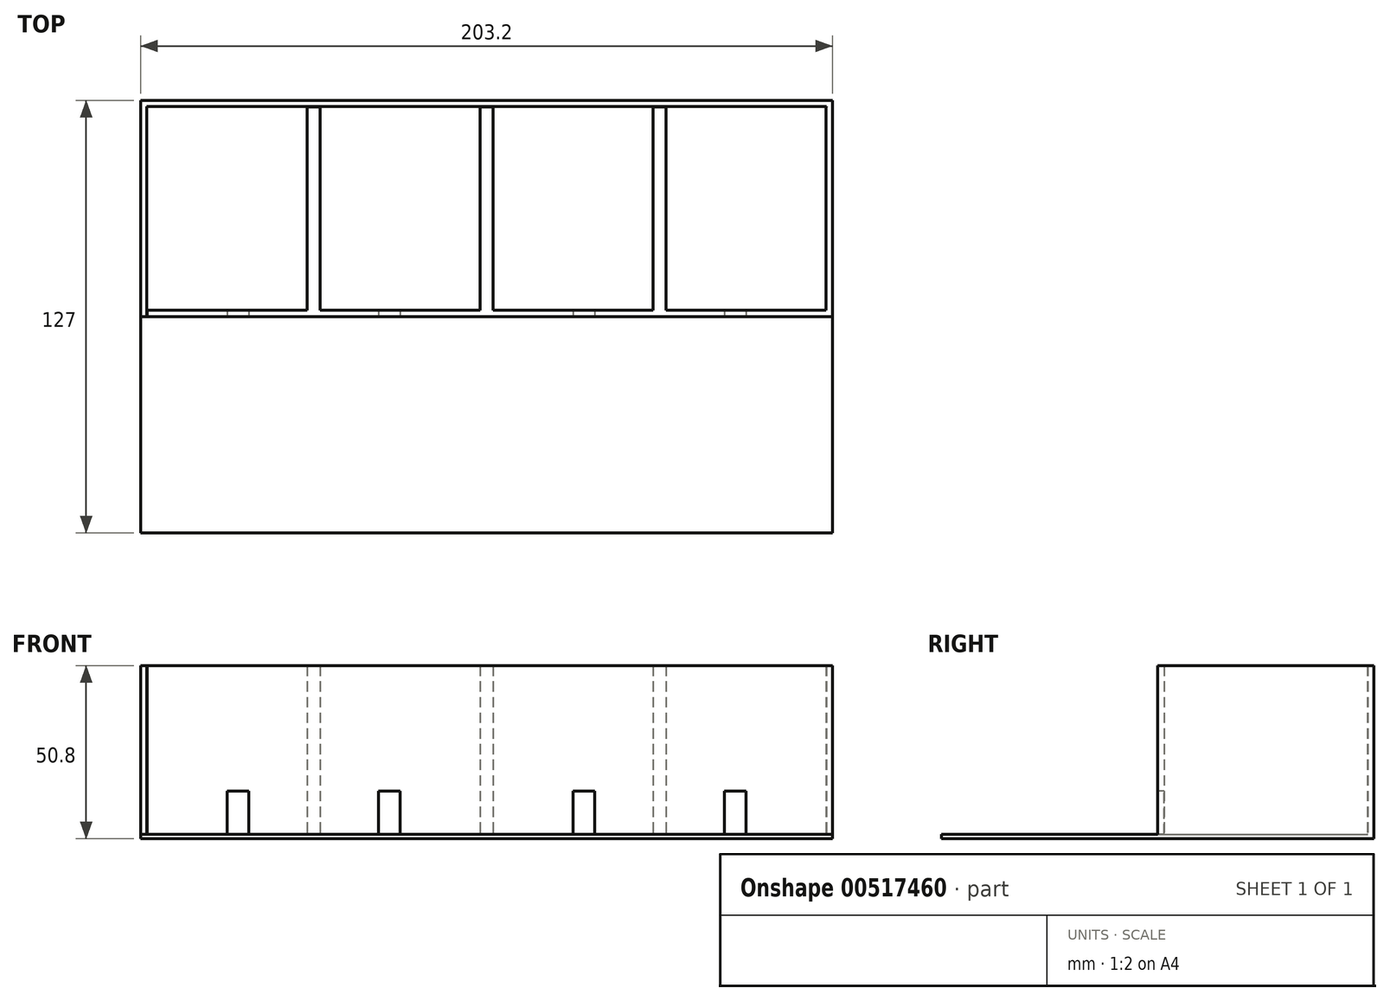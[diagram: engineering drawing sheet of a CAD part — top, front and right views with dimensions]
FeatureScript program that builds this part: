
annotation { "Feature Type Name" : "Feature", "Feature Type Description" : "" }
export const myFeature = defineFeature(function(context is Context, id is Id, definition is map)
    precondition{}
    {
        {
            var Q0;
            Q0=qCreatedBy(makeId("Top.planeOp"),FACE);
            var sketch = newSketch(context, id + "F0", { "sketchPlane" : qUnion([Q0])});
            skLineSegment(sketch, "E0.bottom", {"start": v(0, 0) * mm, "end": v(203.2, 0) * mm});
            skLineSegment(sketch, "E0.top", {"start": v(0, -127) * mm, "end": v(203.2, -127) * mm});
            skLineSegment(sketch, "E0.left", {"start": v(0, 0) * mm, "end": v(0, -127) * mm});
            skLineSegment(sketch, "E0.right", {"start": v(203.2, 0) * mm, "end": v(203.2, -127) * mm});
            skSolve(sketch);
        }
        {
            var Q0;
            Q0=makeQuery(id+"F0.imprint","IMPRINT",FACE,{"disambiguationData":[TD([[makeQuery(id+"F0.imprint","IMPRINT",EDGE,{"derivedFrom":sQuery(id+"F0.wireOp",EDGE,"E0.bottom")}),-1.0]])]});
            extrude(context, id + "F1", {"entities" : qUnion([Q0]), "depth" : 1.27 * mm, "offsetDistance" : 25.4 * mm});
        }
        {
            var Q0;
            Q0=qCreatedBy(makeId("Top.planeOp"),FACE);
            var sketch = newSketch(context, id + "F2", { "sketchPlane" : qUnion([Q0])});
            skLineSegment(sketch, "E1.bottom", {"start": v(0, 0) * mm, "end": v(50.8, 0) * mm});
            skLineSegment(sketch, "E1.top", {"start": v(0, -63.5) * mm, "end": v(50.8, -63.5) * mm});
            skLineSegment(sketch, "E1.left", {"start": v(0, 0) * mm, "end": v(0, -63.5) * mm});
            skLineSegment(sketch, "E1.right", {"start": v(50.8, 0) * mm, "end": v(50.8, -63.5) * mm});
            skLineSegment(sketch, "E2.MirrorCS", {"start": v(0, 63.5) * mm, "end": v(50.8, 63.5) * mm});
            skLineSegment(sketch, "E3.MirrorCS", {"start": v(101.6, -63.5) * mm, "end": v(50.8, -63.5) * mm});
            skLineSegment(sketch, "E4", {"start": v(101.6, -63.5) * mm, "end": v(101.6, 0) * mm});
            skLineSegment(sketch, "E5", {"start": v(101.6, 0) * mm, "end": v(50.8, 0) * mm});
            skLineSegment(sketch, "E6.MirrorCS", {"start": v(101.6, -63.5) * mm, "end": v(152.4, -63.5) * mm});
            skLineSegment(sketch, "E7", {"start": v(152.4, -63.5) * mm, "end": v(152.4, 0) * mm});
            skLineSegment(sketch, "E8", {"start": v(152.4, 0) * mm, "end": v(101.6, 0) * mm});
            skLineSegment(sketch, "E9.MirrorCS", {"start": v(203.2, -63.5) * mm, "end": v(152.4, -63.5) * mm});
            skLineSegment(sketch, "E10", {"start": v(203.2, -63.5) * mm, "end": v(203.2, 0) * mm});
            skLineSegment(sketch, "E11", {"start": v(203.2, 0) * mm, "end": v(152.4, 0) * mm});
            skLineSegment(sketch, "E12.0", {"start": v(0, -61.6) * mm, "end": v(48.9, -61.6) * mm});
            skLineSegment(sketch, "E12.1", {"start": v(48.9, 0) * mm, "end": v(48.9, -61.6) * mm});
            skLineSegment(sketch, "E13.0", {"start": v(-6.35, 6.35) * mm, "end": v(-6.35, -133.35) * mm});
            skLineSegment(sketch, "E13.1", {"start": v(209.55, 6.35) * mm, "end": v(-6.35, 6.35) * mm});
            skLineSegment(sketch, "E13.2", {"start": v(209.55, -133.35) * mm, "end": v(209.55, 6.35) * mm});
            skLineSegment(sketch, "E13.3", {"start": v(-6.35, -133.35) * mm, "end": v(209.55, -133.35) * mm});
            skLineSegment(sketch, "E14.0", {"start": v(99.7, -61.6) * mm, "end": v(99.7, 0) * mm});
            skLineSegment(sketch, "E14.1", {"start": v(99.7, -61.6) * mm, "end": v(52.7, -61.6) * mm});
            skLineSegment(sketch, "E14.2", {"start": v(52.7, 0) * mm, "end": v(52.7, -61.6) * mm});
            skLineSegment(sketch, "E15.0", {"start": v(103.5, -61.6) * mm, "end": v(103.5, 0) * mm});
            skLineSegment(sketch, "E15.1", {"start": v(103.5, -61.6) * mm, "end": v(150.5, -61.6) * mm});
            skLineSegment(sketch, "E15.2", {"start": v(150.5, -61.6) * mm, "end": v(150.5, 0) * mm});
            skLineSegment(sketch, "E16.0", {"start": v(154.3, -61.6) * mm, "end": v(154.3, 0) * mm});
            skLineSegment(sketch, "E16.1", {"start": v(201.3, -61.6) * mm, "end": v(154.3, -61.6) * mm});
            skLineSegment(sketch, "E16.2", {"start": v(201.3, -61.6) * mm, "end": v(201.3, 0) * mm});
            skLineSegment(sketch, "E17.0", {"start": v(1.9, -1.9) * mm, "end": v(1.9, -63.5) * mm});
            skLineSegment(sketch, "E17.1", {"start": v(1.9, -1.9) * mm, "end": v(50.8, -1.9) * mm});
            skLineSegment(sketch, "E18.0", {"start": v(101.6, -1.9) * mm, "end": v(50.8, -1.9) * mm});
            skLineSegment(sketch, "E18.1", {"start": v(152.4, -1.9) * mm, "end": v(101.6, -1.9) * mm});
            skLineSegment(sketch, "E18.2", {"start": v(203.2, -1.9) * mm, "end": v(152.4, -1.9) * mm});
            skLineSegment(sketch, "E19.0", {"start": v(-0.16, 0.16) * mm, "end": v(-0.16, -127.16) * mm});
            skLineSegment(sketch, "E19.1", {"start": v(203.36, 0.16) * mm, "end": v(-0.16, 0.16) * mm});
            skLineSegment(sketch, "E19.2", {"start": v(203.36, -127.16) * mm, "end": v(203.36, 0.16) * mm});
            skLineSegment(sketch, "E19.3", {"start": v(-0.16, -127.16) * mm, "end": v(203.36, -127.16) * mm});
            skLineSegment(sketch, "E20.0", {"start": v(1.74, -125.26) * mm, "end": v(203.36, -125.26) * mm});
            skLineSegment(sketch, "E20.1", {"start": v(1.74, 0.16) * mm, "end": v(1.74, -125.26) * mm});
            skLineSegment(sketch, "E21.0", {"start": v(201.46, -125.26) * mm, "end": v(201.46, -1.74) * mm});
            skLineSegment(sketch, "E21.1", {"start": v(1.74, -125.26) * mm, "end": v(201.46, -125.26) * mm});
            skLineSegment(sketch, "E21.2", {"start": v(1.74, -1.74) * mm, "end": v(1.74, -125.26) * mm});
            skLineSegment(sketch, "E21.3", {"start": v(201.46, -1.74) * mm, "end": v(1.74, -1.74) * mm});
            skLineSegment(sketch, "E22.0", {"start": v(-6.35, -133.35) * mm, "end": v(-6.35, 6.35) * mm});
            skLineSegment(sketch, "E22.1", {"start": v(209.55, -133.35) * mm, "end": v(-6.35, -133.35) * mm});
            skLineSegment(sketch, "E22.2", {"start": v(209.55, 6.35) * mm, "end": v(209.55, -133.35) * mm});
            skLineSegment(sketch, "E22.3", {"start": v(-6.35, 6.35) * mm, "end": v(209.55, 6.35) * mm});
            skSolve(sketch);
        }
        {
            var Q0;
            {var subQ0=sQuery(id+"F2.wireOp",EDGE,"E12.1");var subQ1=sQuery(id+"F2.wireOp",EDGE,"E12.0");var subQ2=makeQuery(id+"F2.imprint","INTERSECT",VERTEX,{"derivedFrom":[subQ1,subQ0]});Q0=makeQuery(id+"F2.imprint","IMPRINT",FACE,{"disambiguationData":[TD([[makeQuery(id+"F2.imprint","IMPRINT",EDGE,{"disambiguationData":[TD([[subQ2,1.0]])],"derivedFrom":subQ1}),-1.0]])]});}
            var Q1;
            {var subQ1=sQuery(id+"F2.wireOp",EDGE,"E1.left");var subQ7=sQuery(id+"F2.wireOp",EDGE,"E1.bottom");var subQ9=makeQuery(id+"F2.imprint","INTERSECT",VERTEX,{"derivedFrom":[subQ7,subQ1]});Q1=makeQuery(id+"F2.imprint","IMPRINT",FACE,{"disambiguationData":[TD([[makeQuery(id+"F2.imprint","IMPRINT",EDGE,{"disambiguationData":[TD([[subQ9,-1.0]])],"derivedFrom":subQ7}),-1.0]])]});}
            var Q2;
            {var subQ5=sQuery(id+"F2.wireOp",EDGE,"E3.MirrorCS");Q2=makeQuery(id+"F2.imprint","IMPRINT",FACE,{"disambiguationData":[TD([[makeQuery(id+"F2.imprint","IMPRINT",EDGE,{"derivedFrom":subQ5}),-1.0]])]});}
            var Q3;
            {var subQ4=sQuery(id+"F2.wireOp",EDGE,"E6.MirrorCS");Q3=makeQuery(id+"F2.imprint","IMPRINT",FACE,{"disambiguationData":[TD([[makeQuery(id+"F2.imprint","IMPRINT",EDGE,{"derivedFrom":subQ4}),1.0]])]});}
            var Q4;
            {var subQ0=sQuery(id+"F2.wireOp",EDGE,"E16.1");Q4=makeQuery(id+"F2.imprint","IMPRINT",FACE,{"disambiguationData":[TD([[makeQuery(id+"F2.imprint","IMPRINT",EDGE,{"derivedFrom":subQ0}),1.0]])]});}
            var Q5;
            {var subQ0=sQuery(id+"F2.wireOp",EDGE,"E10");var subQ1=sQuery(id+"F2.wireOp",EDGE,"E9.MirrorCS");var subQ2=makeQuery(id+"F2.imprint","INTERSECT",VERTEX,{"derivedFrom":[subQ1,subQ0]});Q5=makeQuery(id+"F2.imprint","IMPRINT",FACE,{"disambiguationData":[TD([[makeQuery(id+"F2.imprint","IMPRINT",EDGE,{"disambiguationData":[TD([[subQ2,-1.0]])],"derivedFrom":subQ1}),-1.0]])]});}
            var Q6;
            {var subQ0=sQuery(id+"F2.wireOp",EDGE,"E16.0");var subQ1=sQuery(id+"F2.wireOp",EDGE,"E11");var subQ2=makeQuery(id+"F2.imprint","INTERSECT",VERTEX,{"derivedFrom":[subQ1,subQ0]});Q6=makeQuery(id+"F2.imprint","IMPRINT",FACE,{"disambiguationData":[TD([[makeQuery(id+"F2.imprint","IMPRINT",EDGE,{"disambiguationData":[TD([[subQ2,1.0]])],"derivedFrom":subQ1}),1.0]])]});}
            var Q7;
            {var subQ1=sQuery(id+"F2.wireOp",EDGE,"E10");var subQ6=sQuery(id+"F2.wireOp",EDGE,"E11");var subQ10=makeQuery(id+"F2.imprint","INTERSECT",VERTEX,{"derivedFrom":[subQ1,subQ6]});Q7=makeQuery(id+"F2.imprint","IMPRINT",FACE,{"disambiguationData":[TD([[makeQuery(id+"F2.imprint","IMPRINT",EDGE,{"disambiguationData":[TD([[subQ10,1.0]])],"derivedFrom":subQ1}),1.0]])]});}
            var Q8;
            {var subQ0=sQuery(id+"F2.wireOp",EDGE,"E15.0");var subQ1=sQuery(id+"F2.wireOp",EDGE,"E8");var subQ2=makeQuery(id+"F2.imprint","INTERSECT",VERTEX,{"derivedFrom":[subQ1,subQ0]});Q8=makeQuery(id+"F2.imprint","IMPRINT",FACE,{"disambiguationData":[TD([[makeQuery(id+"F2.imprint","IMPRINT",EDGE,{"disambiguationData":[TD([[subQ2,1.0]])],"derivedFrom":subQ1}),1.0]])]});}
            var Q9;
            {var subQ0=sQuery(id+"F2.wireOp",EDGE,"E8");var subQ5=sQuery(id+"F2.wireOp",EDGE,"E15.2");var subQ6=makeQuery(id+"F2.imprint","INTERSECT",VERTEX,{"derivedFrom":[subQ0,subQ5]});Q9=makeQuery(id+"F2.imprint","IMPRINT",FACE,{"disambiguationData":[TD([[makeQuery(id+"F2.imprint","IMPRINT",EDGE,{"disambiguationData":[TD([[subQ6,1.0]])],"derivedFrom":subQ5}),-1.0]])]});}
            var Q10;
            {var subQ0=sQuery(id+"F2.wireOp",EDGE,"E11");var subQ5=sQuery(id+"F2.wireOp",EDGE,"E16.0");var subQ6=makeQuery(id+"F2.imprint","INTERSECT",VERTEX,{"derivedFrom":[subQ0,subQ5]});Q10=makeQuery(id+"F2.imprint","IMPRINT",FACE,{"disambiguationData":[TD([[makeQuery(id+"F2.imprint","IMPRINT",EDGE,{"disambiguationData":[TD([[subQ6,1.0]])],"derivedFrom":subQ5}),1.0]])]});}
            var Q11;
            {var subQ0=sQuery(id+"F2.wireOp",EDGE,"E14.0");var subQ1=sQuery(id+"F2.wireOp",EDGE,"E5");var subQ2=makeQuery(id+"F2.imprint","INTERSECT",VERTEX,{"derivedFrom":[subQ1,subQ0]});Q11=makeQuery(id+"F2.imprint","IMPRINT",FACE,{"disambiguationData":[TD([[makeQuery(id+"F2.imprint","IMPRINT",EDGE,{"disambiguationData":[TD([[subQ2,-1.0]])],"derivedFrom":subQ1}),1.0]])]});}
            var Q12;
            {var subQ0=sQuery(id+"F2.wireOp",EDGE,"E5");var subQ5=sQuery(id+"F2.wireOp",EDGE,"E14.0");var subQ6=makeQuery(id+"F2.imprint","INTERSECT",VERTEX,{"derivedFrom":[subQ0,subQ5]});Q12=makeQuery(id+"F2.imprint","IMPRINT",FACE,{"disambiguationData":[TD([[makeQuery(id+"F2.imprint","IMPRINT",EDGE,{"disambiguationData":[TD([[subQ6,1.0]])],"derivedFrom":subQ5}),-1.0]])]});}
            var Q13;
            {var subQ0=sQuery(id+"F2.wireOp",EDGE,"E8");var subQ5=sQuery(id+"F2.wireOp",EDGE,"E15.0");var subQ6=makeQuery(id+"F2.imprint","INTERSECT",VERTEX,{"derivedFrom":[subQ0,subQ5]});Q13=makeQuery(id+"F2.imprint","IMPRINT",FACE,{"disambiguationData":[TD([[makeQuery(id+"F2.imprint","IMPRINT",EDGE,{"disambiguationData":[TD([[subQ6,1.0]])],"derivedFrom":subQ5}),1.0]])]});}
            var Q14;
            {var subQ1=sQuery(id+"F2.wireOp",EDGE,"E1.bottom");var subQ3=sQuery(id+"F2.wireOp",EDGE,"E12.1");var subQ4=makeQuery(id+"F2.imprint","INTERSECT",VERTEX,{"derivedFrom":[subQ1,subQ3]});Q14=makeQuery(id+"F2.imprint","IMPRINT",FACE,{"disambiguationData":[TD([[makeQuery(id+"F2.imprint","IMPRINT",EDGE,{"disambiguationData":[TD([[subQ4,-1.0]])],"derivedFrom":subQ3}),1.0]])]});}
            var Q15;
            {var subQ0=sQuery(id+"F2.wireOp",EDGE,"E5");var subQ5=sQuery(id+"F2.wireOp",EDGE,"E14.2");var subQ6=makeQuery(id+"F2.imprint","INTERSECT",VERTEX,{"derivedFrom":[subQ0,subQ5]});Q15=makeQuery(id+"F2.imprint","IMPRINT",FACE,{"disambiguationData":[TD([[makeQuery(id+"F2.imprint","IMPRINT",EDGE,{"disambiguationData":[TD([[subQ6,-1.0]])],"derivedFrom":subQ5}),-1.0]])]});}
            var Q16;
            {var subQ0=sQuery(id+"F2.wireOp",EDGE,"E12.1");var subQ1=sQuery(id+"F2.wireOp",EDGE,"E1.bottom");var subQ2=makeQuery(id+"F2.imprint","INTERSECT",VERTEX,{"derivedFrom":[subQ1,subQ0]});Q16=makeQuery(id+"F2.imprint","IMPRINT",FACE,{"disambiguationData":[TD([[makeQuery(id+"F2.imprint","IMPRINT",EDGE,{"disambiguationData":[TD([[subQ2,1.0]])],"derivedFrom":subQ1}),-1.0]])]});}
            var Q17;
            {var subQ0=sQuery(id+"F2.wireOp",EDGE,"E1.left");var subQ1=sQuery(id+"F2.wireOp",EDGE,"E1.top");var subQ2=makeQuery(id+"F2.imprint","INTERSECT",VERTEX,{"derivedFrom":[subQ1,subQ0]});Q17=makeQuery(id+"F2.imprint","IMPRINT",FACE,{"disambiguationData":[TD([[makeQuery(id+"F2.imprint","IMPRINT",EDGE,{"disambiguationData":[TD([[subQ2,-1.0]])],"derivedFrom":subQ1}),1.0]])]});}
            extrude(context, id + "F3", {"entities" : qUnion([Q0, Q1, Q2, Q3, Q4, Q5, Q6, Q7, Q8, Q9, Q10, Q11, Q12, Q13, Q14, Q15, Q16, Q17]), "operationType" : NewBodyOperationType.ADD, "depth" : 50.8 * mm, "offsetDistance" : 25.4 * mm});
        }
        {
            var Q0;
            Q0=makeQuery(id+"F3.opExtrude","SWEPT_FACE",FACE,{"disambiguationData":[OSD([sQuery(id+"F2.wireOp",EDGE,"E1.top"),sQuery(id+"F2.wireOp",EDGE,"E3.MirrorCS"),sQuery(id+"F2.wireOp",EDGE,"E6.MirrorCS"),sQuery(id+"F2.wireOp",EDGE,"E9.MirrorCS")])]});
            var sketch = newSketch(context, id + "F4", { "sketchPlane" : qUnion([Q0])});
            skLineSegment(sketch, "E23.bottom", {"start": v(25.4, 13.97) * mm, "end": v(31.75, 13.97) * mm});
            skLineSegment(sketch, "E23.top", {"start": v(25.4, 1.27) * mm, "end": v(31.75, 1.27) * mm});
            skLineSegment(sketch, "E23.left", {"start": v(25.4, 13.97) * mm, "end": v(25.4, 1.27) * mm});
            skLineSegment(sketch, "E23.right", {"start": v(31.75, 13.97) * mm, "end": v(31.75, 1.27) * mm});
            skLineSegment(sketch, "E24.bottom", {"start": v(171.45, 13.97) * mm, "end": v(177.8, 13.97) * mm});
            skLineSegment(sketch, "E24.top", {"start": v(171.45, 1.27) * mm, "end": v(177.8, 1.27) * mm});
            skLineSegment(sketch, "E24.left", {"start": v(171.45, 13.97) * mm, "end": v(171.45, 1.27) * mm});
            skLineSegment(sketch, "E24.right", {"start": v(177.8, 13.97) * mm, "end": v(177.8, 1.27) * mm});
            skLineSegment(sketch, "E25.bottom", {"start": v(69.85, 1.27) * mm, "end": v(76.2, 1.27) * mm});
            skLineSegment(sketch, "E25.top", {"start": v(69.85, 13.97) * mm, "end": v(76.2, 13.97) * mm});
            skLineSegment(sketch, "E25.left", {"start": v(69.85, 1.27) * mm, "end": v(69.85, 13.97) * mm});
            skLineSegment(sketch, "E25.right", {"start": v(76.2, 1.27) * mm, "end": v(76.2, 13.97) * mm});
            skLineSegment(sketch, "E26.bottom", {"start": v(133.35, 1.27) * mm, "end": v(127, 1.27) * mm});
            skLineSegment(sketch, "E26.top", {"start": v(133.35, 13.97) * mm, "end": v(127, 13.97) * mm});
            skLineSegment(sketch, "E26.left", {"start": v(133.35, 1.27) * mm, "end": v(133.35, 13.97) * mm});
            skLineSegment(sketch, "E26.right", {"start": v(127, 1.27) * mm, "end": v(127, 13.97) * mm});
            skSolve(sketch);
        }
        {
            var Q0;
            Q0=makeQuery(id+"F4.imprint","IMPRINT",FACE,{"disambiguationData":[TD([[makeQuery(id+"F4.imprint","IMPRINT",EDGE,{"derivedFrom":sQuery(id+"F4.wireOp",EDGE,"E23.bottom")}),-1.0]])]});
            var Q1;
            Q1=makeQuery(id+"F4.imprint","IMPRINT",FACE,{"disambiguationData":[TD([[makeQuery(id+"F4.imprint","IMPRINT",EDGE,{"derivedFrom":sQuery(id+"F4.wireOp",EDGE,"E25.bottom")}),-1.0]])]});
            var Q2;
            Q2=makeQuery(id+"F4.imprint","IMPRINT",FACE,{"disambiguationData":[TD([[makeQuery(id+"F4.imprint","IMPRINT",EDGE,{"derivedFrom":sQuery(id+"F4.wireOp",EDGE,"E26.bottom")}),-1.0]])]});
            var Q3;
            Q3=makeQuery(id+"F4.imprint","IMPRINT",FACE,{"disambiguationData":[TD([[makeQuery(id+"F4.imprint","IMPRINT",EDGE,{"derivedFrom":sQuery(id+"F4.wireOp",EDGE,"E24.bottom")}),-1.0]])]});
            extrude(context, id + "F5", {"entities" : qUnion([Q0, Q1, Q2, Q3]), "operationType" : NewBodyOperationType.REMOVE, "oppositeDirection" : true, "depth" : 25.4 * mm, "offsetDistance" : 25.4 * mm});
        }
    });
